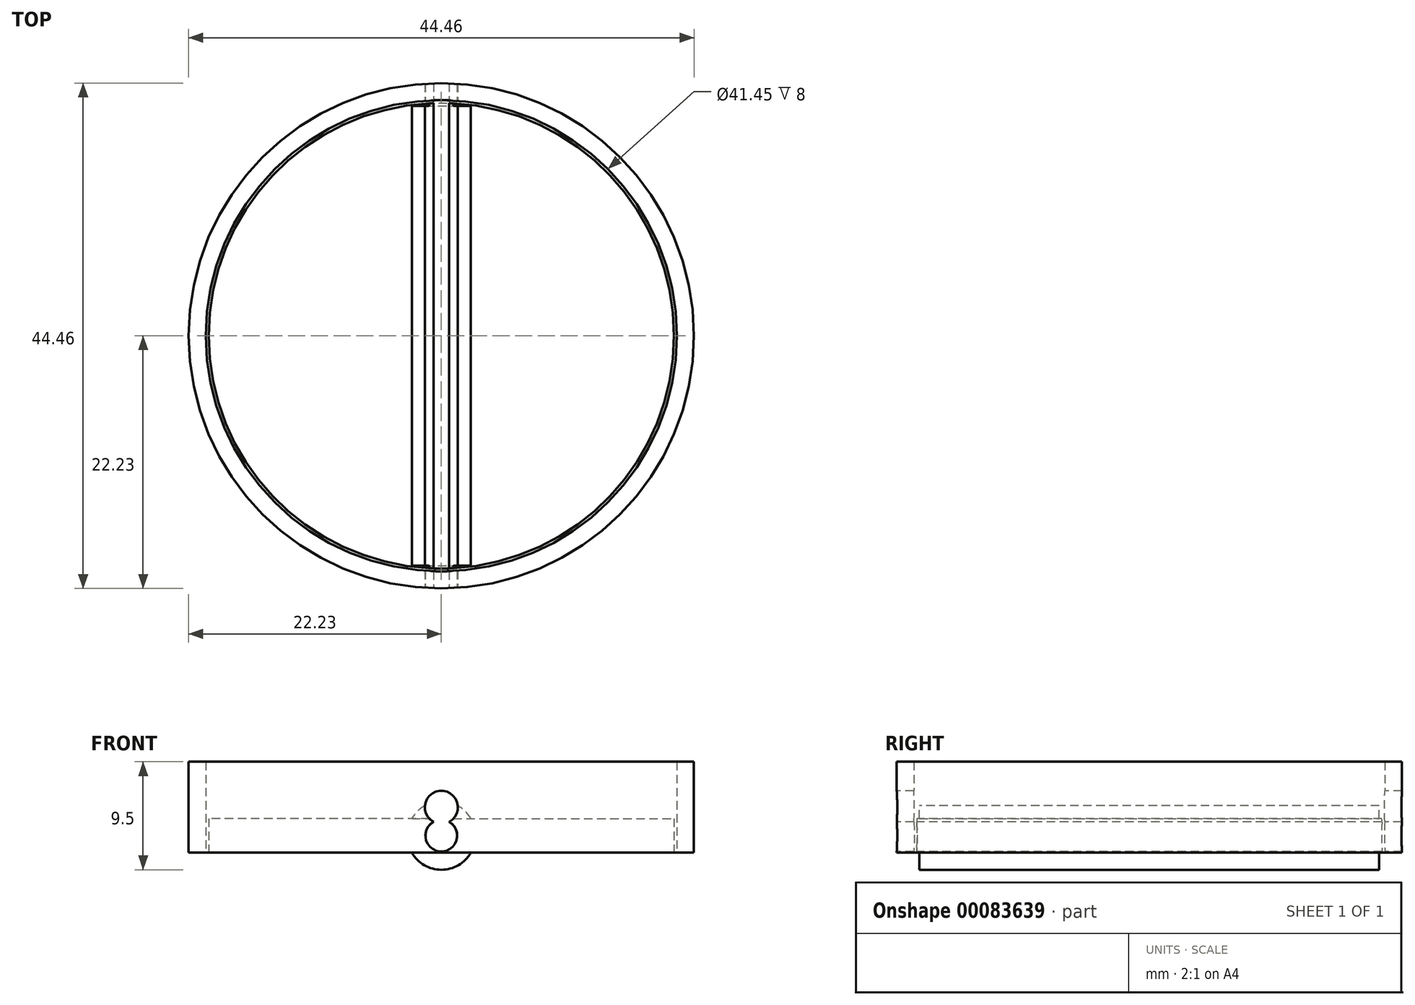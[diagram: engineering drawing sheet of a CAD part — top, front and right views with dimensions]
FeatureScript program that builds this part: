
annotation { "Feature Type Name" : "Feature", "Feature Type Description" : "" }
export const myFeature = defineFeature(function(context is Context, id is Id, definition is map)
    precondition{}
    {
        {
            var Q0;
            Q0=qCreatedBy(makeId("Top.planeOp"),FACE);
            var sketch = newSketch(context, id + "F0", { "sketchPlane" : qUnion([Q0])});
            skCircle(sketch, "E0", {"center": v(0, 0) * mm, "radius": 22.23 * mm});
            skCircle(sketch, "E1", {"center": v(0, 0) * mm, "radius": 20.73 * mm});
            skCircle(sketch, "E2", {"center": v(0, 0) * mm, "radius": 20.48 * mm});
            skSolve(sketch);
        }
        {
            var Q0;
            Q0=makeQuery(id+"F0.imprint","IMPRINT",FACE,{"disambiguationData":[TD([[makeQuery(id+"F0.imprint","IMPRINT",EDGE,{"derivedFrom":sQuery(id+"F0.wireOp",EDGE,"E0")}),1.0]])]});
            extrude(context, id + "F1", {"entities" : qUnion([Q0]), "depth" : 8 * mm});
        }
        {
            var Q0;
            Q0=makeQuery(id+"F0.imprint","IMPRINT",FACE,{"disambiguationData":[TD([[makeQuery(id+"F0.imprint","IMPRINT",EDGE,{"derivedFrom":sQuery(id+"F0.wireOp",EDGE,"E2")}),1.0]])]});
            extrude(context, id + "F2", {"entities" : qUnion([Q0]), "depth" : 3 * mm});
        }
        {
            var Q0;
            Q0=qCreatedBy(makeId("Front.planeOp"),FACE);
            var sketch = newSketch(context, id + "F3", { "sketchPlane" : qUnion([Q0])});
            skCircle(sketch, "E3", {"center": v(0, 1.5) * mm, "radius": 3 * mm});
            skSolve(sketch);
        }
        {
            var Q0;
            Q0 = qSketchRegion(id + "F3", true);
            extrude(context, id + "F4", {"entities" : qUnion([Q0]), "operationType" : NewBodyOperationType.ADD, "depth" : 22.22 * mm - 2 * mm, "hasSecondDirection" : true, "secondDirectionOppositeDirection" : true, "secondDirectionDepth" : 22.22 * mm - 2 * mm});
        }
        {
            var Q0;
            Q0=qCreatedBy(makeId("Front.planeOp"),FACE);
            var sketch = newSketch(context, id + "F5", { "sketchPlane" : qUnion([Q0])});
            skCircle(sketch, "E4", {"center": v(0, 4) * mm, "radius": 1.45 * mm});
            skSolve(sketch);
        }
        {
            var Q0;
            Q0=makeQuery(id+"F5.imprint","IMPRINT",FACE,{"disambiguationData":[TD([[makeQuery(id+"F5.imprint","IMPRINT",EDGE,{"derivedFrom":sQuery(id+"F5.wireOp",EDGE,"E4")}),1.0]])]});
            var Q1;
            Q1=sQuery(id+"F5.wireOp",EDGE,"E4");
            extrude(context, id + "F6", {"entities" : qUnion([Q0]), "operationType" : NewBodyOperationType.REMOVE, "surfaceEntities" : qUnion([Q1]), "endBound" : BoundingType.THROUGH_ALL, "oppositeDirection" : true, "depth" : 25.4 * mm, "hasSecondDirection" : true, "secondDirectionBound" : SecondDirectionBoundingType.THROUGH_ALL, "secondDirectionOppositeDirection" : false, "secondDirectionDepth" : 25.4 * mm});
        }
        {
            var Q0;
            Q0=qCreatedBy(makeId("Front.planeOp"),FACE);
            var sketch = newSketch(context, id + "F7", { "sketchPlane" : qUnion([Q0])});
            skCircle(sketch, "E5", {"center": v(0, 1.5) * mm, "radius": 1.4 * mm});
            skSolve(sketch);
        }
        {
            var Q0;
            Q0 = qSketchRegion(id + "F7", true);
            extrude(context, id + "F8", {"entities" : qUnion([Q0]), "operationType" : NewBodyOperationType.REMOVE, "endBound" : BoundingType.THROUGH_ALL, "oppositeDirection" : true, "depth" : 25.4 * mm, "hasSecondDirection" : true, "secondDirectionBound" : SecondDirectionBoundingType.THROUGH_ALL, "secondDirectionOppositeDirection" : false, "secondDirectionDepth" : 25.4 * mm});
        }
    });
